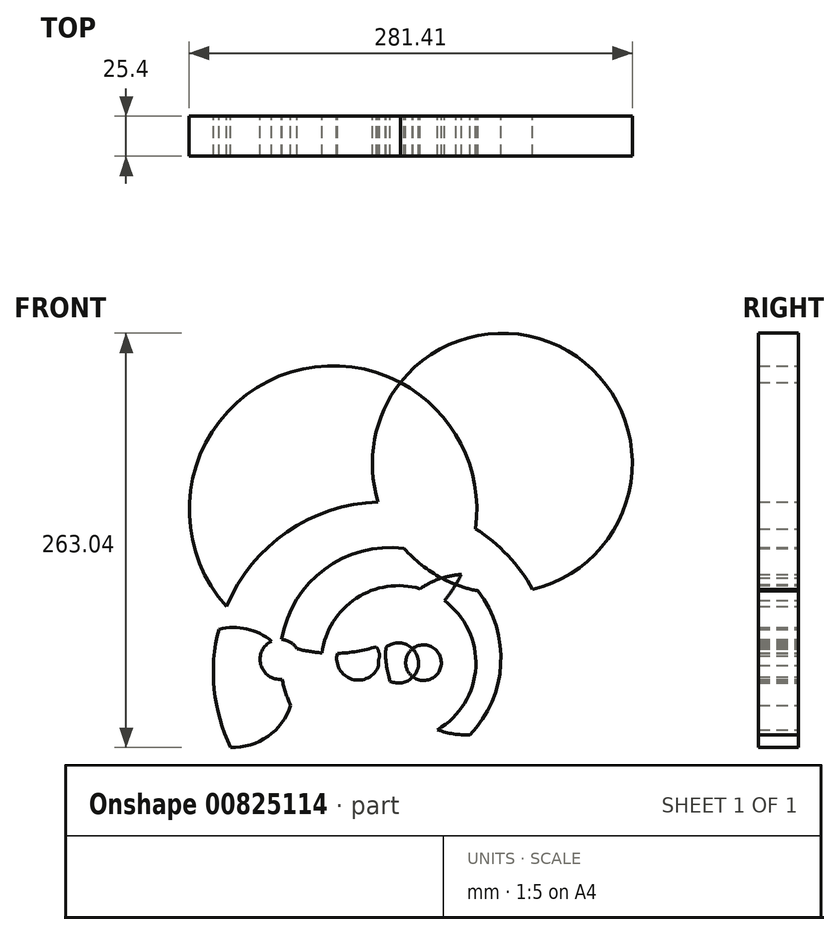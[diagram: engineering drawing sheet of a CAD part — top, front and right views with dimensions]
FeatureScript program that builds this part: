
annotation { "Feature Type Name" : "Feature", "Feature Type Description" : "" }
export const myFeature = defineFeature(function(context is Context, id is Id, definition is map)
    precondition{}
    {
        {
            var Q0;
            Q0=qCreatedBy(makeId("Front.planeOp"),FACE);
            var sketch = newSketch(context, id + "F0", { "sketchPlane" : qUnion([Q0])});
            skCircle(sketch, "E0", {"center": v(0, 0) * mm, "radius": 108.22 * mm});
            skCircle(sketch, "E1", {"center": v(52.25, 11.2) * mm, "radius": 50.98 * mm});
            skCircle(sketch, "E2", {"center": v(25.29, 6.08) * mm, "radius": 11.31 * mm});
            skCircle(sketch, "E3", {"center": v(9.43, 5.9) * mm, "radius": 12.75 * mm});
            skCircle(sketch, "E4", {"center": v(9.43, 5.9) * mm, "radius": 49.1 * mm});
            skCircle(sketch, "E5", {"center": v(-16.13, 8.72) * mm, "radius": 13.68 * mm});
            skCircle(sketch, "E6", {"center": v(4.32, 9.08) * mm, "radius": 70.14 * mm});
            skCircle(sketch, "E7", {"center": v(-65.82, 8.16) * mm, "radius": 12.7 * mm});
            skCircle(sketch, "E8", {"center": v(-95.43, -9.6) * mm, "radius": 38.1 * mm});
            skCircle(sketch, "E9", {"center": v(75.34, 132.8) * mm, "radius": 82.55 * mm});
            skCircle(sketch, "E10", {"center": v(-32.18, 103.33) * mm, "radius": 91.34 * mm});
            skSolve(sketch);
        }
        {
            var Q0;
            {var subQ0=sQuery(id+"F0.wireOp",EDGE,"E10");var subQ1=sQuery(id+"F0.wireOp",EDGE,"E0");var subQ2=makeQuery(id+"F0.imprint","INTERSECT",VERTEX,{"disambiguationData":[OD(0.0)],"derivedFrom":[subQ1,subQ0]});Q0=makeQuery(id+"F0.imprint","IMPRINT",FACE,{"disambiguationData":[TD([[makeQuery(id+"F0.imprint","IMPRINT",EDGE,{"disambiguationData":[TD([[subQ2,1.0]])],"derivedFrom":subQ1}),-1.0]])]});}
            var Q1;
            {var subQ0=sQuery(id+"F0.wireOp",EDGE,"E9");var subQ1=sQuery(id+"F0.wireOp",EDGE,"E0");var subQ2=makeQuery(id+"F0.imprint","INTERSECT",VERTEX,{"disambiguationData":[OD(0.0)],"derivedFrom":[subQ1,subQ0]});Q1=makeQuery(id+"F0.imprint","IMPRINT",FACE,{"disambiguationData":[TD([[makeQuery(id+"F0.imprint","IMPRINT",EDGE,{"disambiguationData":[TD([[subQ2,-1.0]])],"derivedFrom":subQ1}),-1.0]])]});}
            var Q2;
            {var subQ1=sQuery(id+"F0.wireOp",EDGE,"E1");var subQ5=sQuery(id+"F0.wireOp",EDGE,"E4");var subQ6=makeQuery(id+"F0.imprint","INTERSECT",VERTEX,{"disambiguationData":[OD(1.0)],"derivedFrom":[subQ1,subQ5]});Q2=makeQuery(id+"F0.imprint","IMPRINT",FACE,{"disambiguationData":[TD([[makeQuery(id+"F0.imprint","IMPRINT",EDGE,{"disambiguationData":[TD([[subQ6,-1.0]])],"derivedFrom":subQ1}),1.0]])]});}
            var Q3;
            {var subQ0=sQuery(id+"F0.wireOp",EDGE,"E5");var subQ1=sQuery(id+"F0.wireOp",EDGE,"E3");var subQ2=makeQuery(id+"F0.imprint","INTERSECT",VERTEX,{"disambiguationData":[OD(0.0)],"derivedFrom":[subQ1,subQ0]});Q3=makeQuery(id+"F0.imprint","IMPRINT",FACE,{"disambiguationData":[TD([[makeQuery(id+"F0.imprint","IMPRINT",EDGE,{"disambiguationData":[TD([[subQ2,-1.0]])],"derivedFrom":subQ1}),-1.0]])]});}
            var Q4;
            {var subQ5=sQuery(id+"F0.wireOp",EDGE,"E9");var subQ6=sQuery(id+"F0.wireOp",EDGE,"E1");var subQ7=makeQuery(id+"F0.imprint","INTERSECT",VERTEX,{"disambiguationData":[OD(1.0)],"derivedFrom":[subQ6,subQ5]});Q4=makeQuery(id+"F0.imprint","IMPRINT",FACE,{"disambiguationData":[TD([[makeQuery(id+"F0.imprint","IMPRINT",EDGE,{"disambiguationData":[TD([[subQ7,-1.0]])],"derivedFrom":subQ6}),-1.0]])]});}
            var Q5;
            {var subQ0=sQuery(id+"F0.wireOp",EDGE,"E8");var subQ7=sQuery(id+"F0.wireOp",EDGE,"E0");var subQ8=makeQuery(id+"F0.imprint","INTERSECT",VERTEX,{"disambiguationData":[OD(0.0)],"derivedFrom":[subQ7,subQ0]});Q5=makeQuery(id+"F0.imprint","IMPRINT",FACE,{"disambiguationData":[TD([[makeQuery(id+"F0.imprint","IMPRINT",EDGE,{"disambiguationData":[TD([[subQ8,-1.0]])],"derivedFrom":subQ7}),1.0]])]});}
            var Q6;
            {var subQ0=sQuery(id+"F0.wireOp",EDGE,"E3");var subQ1=sQuery(id+"F0.wireOp",EDGE,"E1");var subQ2=makeQuery(id+"F0.imprint","INTERSECT",VERTEX,{"disambiguationData":[OD(0.0)],"derivedFrom":[subQ1,subQ0]});Q6=makeQuery(id+"F0.imprint","IMPRINT",FACE,{"disambiguationData":[TD([[makeQuery(id+"F0.imprint","IMPRINT",EDGE,{"disambiguationData":[TD([[subQ2,-1.0]])],"derivedFrom":subQ1}),1.0]])]});}
            var Q7;
            {var subQ0=sQuery(id+"F0.wireOp",EDGE,"E3");var subQ1=sQuery(id+"F0.wireOp",EDGE,"E2");var subQ2=makeQuery(id+"F0.imprint","INTERSECT",VERTEX,{"disambiguationData":[OD(0.0)],"derivedFrom":[subQ1,subQ0]});Q7=makeQuery(id+"F0.imprint","IMPRINT",FACE,{"disambiguationData":[TD([[makeQuery(id+"F0.imprint","IMPRINT",EDGE,{"disambiguationData":[TD([[subQ2,1.0]])],"derivedFrom":subQ1}),1.0]])]});}
            var Q8;
            {var subQ0=sQuery(id+"F0.wireOp",EDGE,"E10");var subQ1=sQuery(id+"F0.wireOp",EDGE,"E1");var subQ2=makeQuery(id+"F0.imprint","INTERSECT",VERTEX,{"disambiguationData":[OD(0.0)],"derivedFrom":[subQ1,subQ0]});Q8=makeQuery(id+"F0.imprint","IMPRINT",FACE,{"disambiguationData":[TD([[makeQuery(id+"F0.imprint","IMPRINT",EDGE,{"disambiguationData":[TD([[subQ2,-1.0]])],"derivedFrom":subQ1}),1.0]])]});}
            extrude(context, id + "F1", {"entities" : qUnion([Q0, Q1, Q2, Q3, Q4, Q5, Q6, Q7, Q8]), "depth" : 25.4 * mm, "offsetDistance" : 25.4 * mm});
        }
    });
